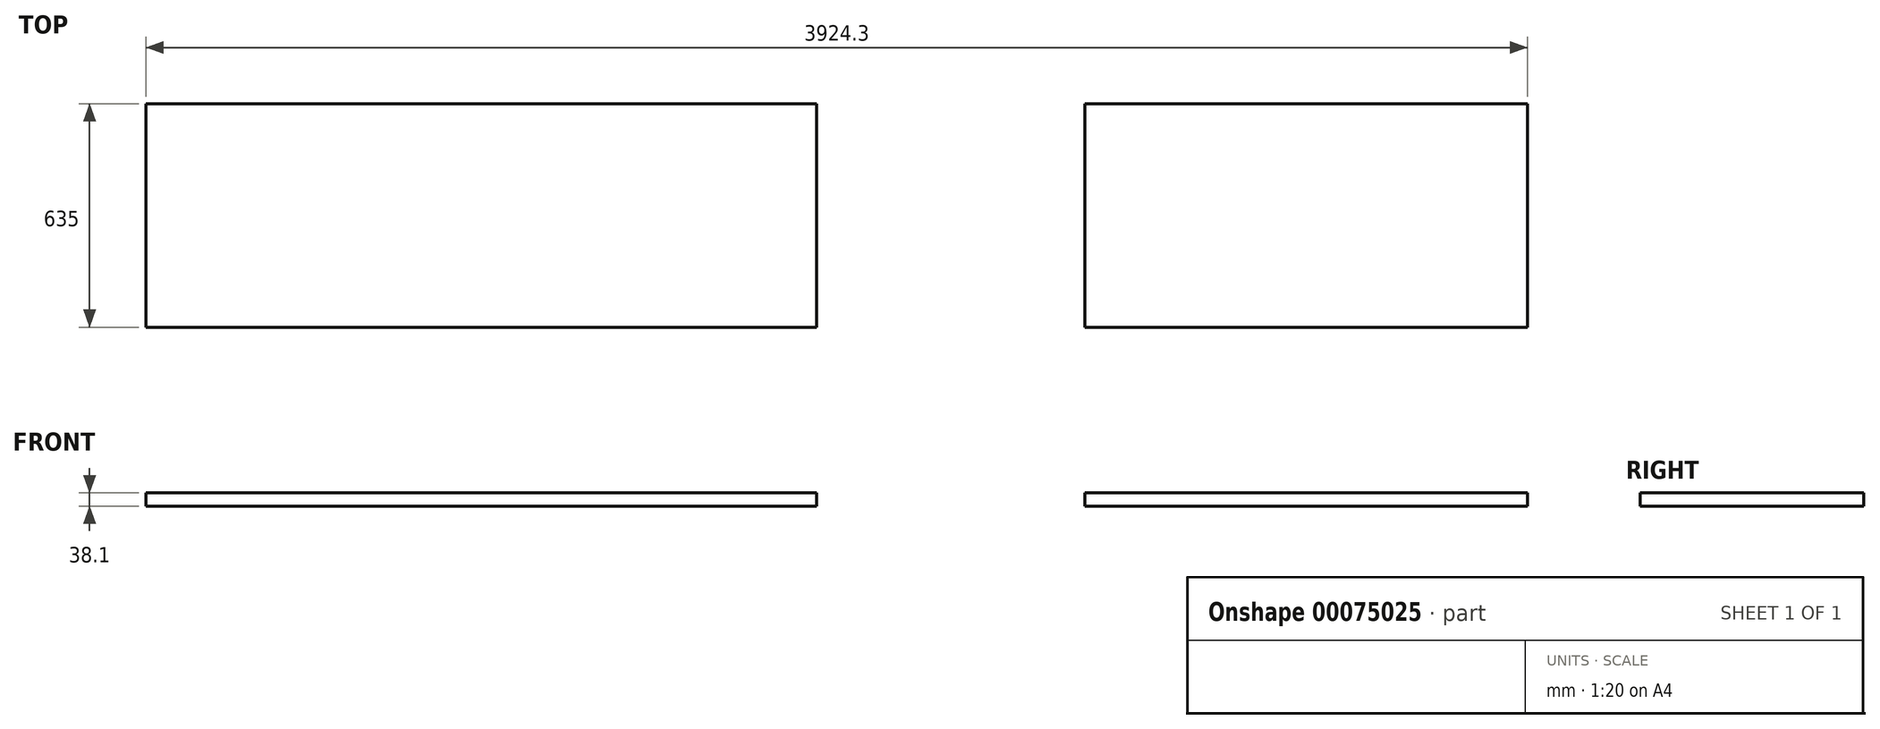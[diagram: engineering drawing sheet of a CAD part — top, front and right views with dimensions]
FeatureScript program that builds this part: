
annotation { "Feature Type Name" : "Feature", "Feature Type Description" : "" }
export const myFeature = defineFeature(function(context is Context, id is Id, definition is map)
    precondition{}
    {
        {
            var Q0;
            Q0=qCreatedBy(makeId("Top.planeOp"),FACE);
            var sketch = newSketch(context, id + "F0", { "sketchPlane" : qUnion([Q0])});
            skLineSegment(sketch, "E0.rect.bottom", {"start": v(1943.1, 317.5) * mm, "end": v(-1943.1, 317.5) * mm});
            skLineSegment(sketch, "E0.rect.top", {"start": v(1943.1, -317.5) * mm, "end": v(-1943.1, -317.5) * mm});
            skLineSegment(sketch, "E0.rect.left", {"start": v(1943.1, 317.5) * mm, "end": v(1943.1, -317.5) * mm});
            skLineSegment(sketch, "E0.rect.right", {"start": v(-1943.1, 317.5) * mm, "end": v(-1943.1, -317.5) * mm});
            skPoint(sketch, "E0.rect.middle", {"position": v(0, 0) * mm});
            skLineSegment(sketch, "E1.bottom", {"start": v(1943.1, 317.5) * mm, "end": v(1981.2, 317.5) * mm});
            skLineSegment(sketch, "E1.top", {"start": v(1943.1, -317.5) * mm, "end": v(1981.2, -317.5) * mm});
            skLineSegment(sketch, "E1.right", {"start": v(1981.2, 317.5) * mm, "end": v(1981.2, -317.5) * mm});
            skLineSegment(sketch, "E2.bottom", {"start": v(-1943.1, -317.5) * mm, "end": v(-1308.1, -317.5) * mm});
            skLineSegment(sketch, "E2.top", {"start": v(-1943.1, -2139.95) * mm, "end": v(-1308.1, -2139.95) * mm});
            skLineSegment(sketch, "E2.left", {"start": v(-1943.1, -317.5) * mm, "end": v(-1943.1, -2139.95) * mm});
            skLineSegment(sketch, "E2.right", {"start": v(-1308.1, -317.5) * mm, "end": v(-1308.1, -2139.95) * mm});
            skLineSegment(sketch, "E3", {"start": v(-1308.1, -568.95) * mm, "end": v(-1056.65, -317.5) * mm});
            skSolve(sketch);
        }
        {
            var Q0;
            Q0=makeQuery(id+"F0.imprint","IMPRINT",FACE,{"disambiguationData":[TD([[makeQuery(id+"F0.imprint","IMPRINT",EDGE,{"derivedFrom":sQuery(id+"F0.wireOp",EDGE,"E0.rect.bottom")}),1.0]])]});
            var Q1;
            Q1=makeQuery(id+"F0.imprint","IMPRINT",FACE,{"disambiguationData":[TD([[makeQuery(id+"F0.imprint","IMPRINT",EDGE,{"derivedFrom":sQuery(id+"F0.wireOp",EDGE,"E2.bottom")}),-1.0]])]});
            var Q2;
            Q2=makeQuery(id+"F0.imprint","IMPRINT",FACE,{"disambiguationData":[TD([[makeQuery(id+"F0.imprint","IMPRINT",EDGE,{"derivedFrom":sQuery(id+"F0.wireOp",EDGE,"E1.bottom")}),-1.0]])]});
            var Q3;
            {var subQ3=sQuery(id+"F0.wireOp",EDGE,"E3");Q3=makeQuery(id+"F0.imprint","IMPRINT",FACE,{"disambiguationData":[TD([[makeQuery(id+"F0.imprint","IMPRINT",EDGE,{"derivedFrom":subQ3}),1.0]])]});}
            extrude(context, id + "F1", {"entities" : qUnion([Q0, Q1, Q2, Q3]), "depth" : 38.1 * mm});
        }
        {
            var Q0;
            Q0=makeQuery(id+"F0.imprint","IMPRINT",FACE,{"disambiguationData":[TD([[makeQuery(id+"F0.imprint","IMPRINT",EDGE,{"derivedFrom":sQuery(id+"F0.wireOp",EDGE,"E1.bottom")}),-1.0]])]});
            extrude(context, id + "F2", {"entities" : qUnion([Q0]), "operationType" : NewBodyOperationType.ADD, "oppositeDirection" : true, "depth" : 876.3 * mm});
        }
        {
            var Q0;
            Q0=makeQuery(id+"F1.opExtrude","CAP_FACE",FACE,{"disambiguationData":[OSD([sQuery(id+"F0.wireOp",EDGE,"E0.rect.bottom"),sQuery(id+"F0.wireOp",EDGE,"E0.rect.top"),sQuery(id+"F0.wireOp",EDGE,"E0.rect.right"),sQuery(id+"F0.wireOp",EDGE,"E1.bottom"),sQuery(id+"F0.wireOp",EDGE,"E1.top"),sQuery(id+"F0.wireOp",EDGE,"E1.right"),sQuery(id+"F0.wireOp",EDGE,"E2.top"),sQuery(id+"F0.wireOp",EDGE,"E2.left"),sQuery(id+"F0.wireOp",EDGE,"E2.right")])],"isStart":false});
            var sketch = newSketch(context, id + "F3", { "sketchPlane" : qUnion([Q0])});
            skLineSegment(sketch, "E4.bottom", {"start": v(-1943.1, -2139.95) * mm, "end": v(-1905, -2139.95) * mm});
            skLineSegment(sketch, "E4.top", {"start": v(-1943.1, 317.5) * mm, "end": v(-1905, 317.5) * mm});
            skLineSegment(sketch, "E4.left", {"start": v(-1943.1, -2139.95) * mm, "end": v(-1943.1, 317.5) * mm});
            skLineSegment(sketch, "E4.right", {"start": v(-1905, -2101.85) * mm, "end": v(-1905, 279.4) * mm});
            skLineSegment(sketch, "E5.bottom", {"start": v(-1943.1, 317.5) * mm, "end": v(1981.2, 317.5) * mm});
            skLineSegment(sketch, "E5.top", {"start": v(-1905, 279.4) * mm, "end": v(1981.2, 279.4) * mm});
            skLineSegment(sketch, "E5.left", {"start": v(-1943.1, 317.5) * mm, "end": v(-1943.1, 279.4) * mm});
            skLineSegment(sketch, "E5.right", {"start": v(1981.2, 317.5) * mm, "end": v(1981.2, 279.4) * mm});
            skLineSegment(sketch, "E6.bottom", {"start": v(-1905, -2139.95) * mm, "end": v(-1308.1, -2139.95) * mm});
            skLineSegment(sketch, "E6.top", {"start": v(-1905, -2101.85) * mm, "end": v(-1308.1, -2101.85) * mm});
            skLineSegment(sketch, "E6.right", {"start": v(-1308.1, -2139.95) * mm, "end": v(-1308.1, -2101.85) * mm});
            skSolve(sketch);
        }
        {
            var Q0;
            Q0=makeQuery(id+"F1.opExtrude","CAP_FACE",FACE,{"disambiguationData":[OSD([sQuery(id+"F0.wireOp",EDGE,"E0.rect.bottom"),sQuery(id+"F0.wireOp",EDGE,"E0.rect.top"),sQuery(id+"F0.wireOp",EDGE,"E0.rect.right"),sQuery(id+"F0.wireOp",EDGE,"E1.bottom"),sQuery(id+"F0.wireOp",EDGE,"E1.top"),sQuery(id+"F0.wireOp",EDGE,"E1.right"),sQuery(id+"F0.wireOp",EDGE,"E2.top"),sQuery(id+"F0.wireOp",EDGE,"E2.left"),sQuery(id+"F0.wireOp",EDGE,"E2.right"),sQuery(id+"F0.wireOp",EDGE,"E3")])],"isStart":false});
            var sketch = newSketch(context, id + "F4", { "sketchPlane" : qUnion([Q0])});
            skLineSegment(sketch, "E7.bottom", {"start": v(723.9, -317.5) * mm, "end": v(-38.1, -317.5) * mm});
            skLineSegment(sketch, "E7.top", {"start": v(723.9, 489.68) * mm, "end": v(-38.1, 489.68) * mm});
            skLineSegment(sketch, "E7.left", {"start": v(723.9, -317.5) * mm, "end": v(723.9, 489.68) * mm});
            skLineSegment(sketch, "E7.right", {"start": v(-38.1, -317.5) * mm, "end": v(-38.1, 489.68) * mm});
            skSolve(sketch);
        }
        {
            var Q0;
            Q0=qSketchRegion(id+"F4",true);
            extrude(context, id + "F5", {"entities" : qUnion([Q0]), "operationType" : NewBodyOperationType.REMOVE, "oppositeDirection" : true, "depth" : 203.2 * mm, "hasSecondDirection" : true, "secondDirectionOppositeDirection" : false, "secondDirectionDepth" : 203.2 * mm});
        }
        {
            var Q0;
            {var subQ0=sQuery(id+"F0.wireOp",EDGE,"E1.top");var subQ1=sQuery(id+"F0.wireOp",EDGE,"E2.right");var subQ2=sQuery(id+"F0.wireOp",EDGE,"E3");var subQ3=sQuery(id+"F0.wireOp",EDGE,"E0.rect.top");Q0=makeQuery(id+"F5.boolean.opBoolean","SPLIT",FACE,{"disambiguationData":[TD([makeQuery(id+"F1.opExtrude","SWEPT_FACE",FACE,{"disambiguationData":[OSD([subQ1])]})])],"derivedFrom":makeQuery(id+"F1.opExtrude","CAP_FACE",FACE,{"disambiguationData":[OSD([sQuery(id+"F0.wireOp",EDGE,"E0.rect.bottom"),subQ3,sQuery(id+"F0.wireOp",EDGE,"E0.rect.right"),sQuery(id+"F0.wireOp",EDGE,"E1.bottom"),subQ0,sQuery(id+"F0.wireOp",EDGE,"E1.right"),sQuery(id+"F0.wireOp",EDGE,"E2.top"),sQuery(id+"F0.wireOp",EDGE,"E2.left"),subQ1,subQ2])],"isStart":false})});}
            var sketch = newSketch(context, id + "F6", { "sketchPlane" : qUnion([Q0])});
            skLineSegment(sketch, "E8.rect.bottom", {"start": v(-1460.5, -647.7) * mm, "end": v(-1714.5, -647.7) * mm});
            skLineSegment(sketch, "E8.rect.top", {"start": v(-1460.5, -1460.5) * mm, "end": v(-1714.5, -1460.5) * mm});
            skLineSegment(sketch, "E8.rect.left", {"start": v(-1358.9, -749.3) * mm, "end": v(-1358.9, -1358.9) * mm});
            skLineSegment(sketch, "E8.rect.right", {"start": v(-1816.1, -749.3) * mm, "end": v(-1816.1, -1358.9) * mm});
            skPoint(sketch, "E8.rect.middle", {"position": v(-1587.5, -1054.1) * mm});
            skPoint(sketch, "E9.visualSharp", {"position": v(-1816.1, -1460.5) * mm});
            skArc(sketch, "E9.filletArc", {"start": v(-1816.1, -1358.9) * mm, "mid": v(-1786.34, -1430.74) * mm, "end": v(-1714.5, -1460.5) * mm});
            skPoint(sketch, "E10.visualSharp", {"position": v(-1358.9, -1460.5) * mm});
            skArc(sketch, "E10.filletArc", {"start": v(-1460.5, -1460.5) * mm, "mid": v(-1388.66, -1430.74) * mm, "end": v(-1358.9, -1358.9) * mm});
            skPoint(sketch, "E11.visualSharp", {"position": v(-1816.1, -647.7) * mm});
            skArc(sketch, "E11.filletArc", {"start": v(-1714.5, -647.7) * mm, "mid": v(-1786.34, -677.46) * mm, "end": v(-1816.1, -749.3) * mm});
            skPoint(sketch, "E12.visualSharp", {"position": v(-1358.9, -647.7) * mm});
            skArc(sketch, "E12.filletArc", {"start": v(-1358.9, -749.3) * mm, "mid": v(-1388.66, -677.46) * mm, "end": v(-1460.5, -647.7) * mm});
            skLineSegment(sketch, "E13", {"start": v(-1587.5, -1054.1) * mm, "end": v(-1854.2, -1054.1) * mm, "construction": true});
            skPoint(sketch, "E13.endSnap0", {"position": v(-1816.1, -1054.1) * mm});
            skCircle(sketch, "E14", {"center": v(-1854.2, -1054.1) * mm, "radius": 12.7 * mm});
            skSolve(sketch);
        }
        {
            var Q0;
            Q0=qSketchRegion(id+"F6",true);
            extrude(context, id + "F7", {"entities" : qUnion([Q0]), "operationType" : NewBodyOperationType.REMOVE, "oppositeDirection" : true, "depth" : 127 * mm});
        }
        {
            var Q0;
            Q0=makeQuery(id+"F2.opExtrude","SWEPT_FACE",FACE,{"disambiguationData":[OSD([sQuery(id+"F0.wireOp",EDGE,"E0.rect.left")])]});
            extrude(context, id + "F8", {"entities" : qUnion([Q0]), "operationType" : NewBodyOperationType.REMOVE, "oppositeDirection" : true, "depth" : 127 * mm});
        }
        {
            var Q0;
            {var subQ0=sQuery(id+"F0.wireOp",EDGE,"E1.top");var subQ1=sQuery(id+"F0.wireOp",EDGE,"E2.right");var subQ2=sQuery(id+"F0.wireOp",EDGE,"E3");var subQ3=sQuery(id+"F0.wireOp",EDGE,"E0.rect.top");Q0=makeQuery(id+"F5.boolean.opBoolean","SPLIT",FACE,{"disambiguationData":[TD([makeQuery(id+"F1.opExtrude","SWEPT_FACE",FACE,{"disambiguationData":[OSD([subQ1])]})])],"derivedFrom":makeQuery(id+"F1.opExtrude","CAP_FACE",FACE,{"disambiguationData":[OSD([sQuery(id+"F0.wireOp",EDGE,"E0.rect.bottom"),subQ3,sQuery(id+"F0.wireOp",EDGE,"E0.rect.right"),sQuery(id+"F0.wireOp",EDGE,"E1.bottom"),subQ0,sQuery(id+"F0.wireOp",EDGE,"E1.right"),sQuery(id+"F0.wireOp",EDGE,"E2.top"),sQuery(id+"F0.wireOp",EDGE,"E2.left"),subQ1,subQ2])],"isStart":false})});}
            var sketch = newSketch(context, id + "F9", { "sketchPlane" : qUnion([Q0])});
            skLineSegment(sketch, "E15.rect.bottom", {"start": v(-1308.1, -977.27) * mm, "end": v(-858.66, -977.27) * mm});
            skLineSegment(sketch, "E15.rect.top", {"start": v(-1308.1, -317.5) * mm, "end": v(-858.66, -317.5) * mm});
            skLineSegment(sketch, "E15.rect.left", {"start": v(-1308.1, -977.27) * mm, "end": v(-1308.1, -317.5) * mm});
            skLineSegment(sketch, "E15.rect.right", {"start": v(-858.66, -977.27) * mm, "end": v(-858.66, -317.5) * mm});
            skPoint(sketch, "E15.rect.middle", {"position": v(-1083.38, -647.39) * mm});
            skSolve(sketch);
        }
        {
            var Q0;
            Q0 = qSketchRegion(id + "F9", true);
            extrude(context, id + "F10", {"entities" : qUnion([Q0]), "operationType" : NewBodyOperationType.REMOVE, "oppositeDirection" : true, "depth" : 127 * mm});
        }
    });
